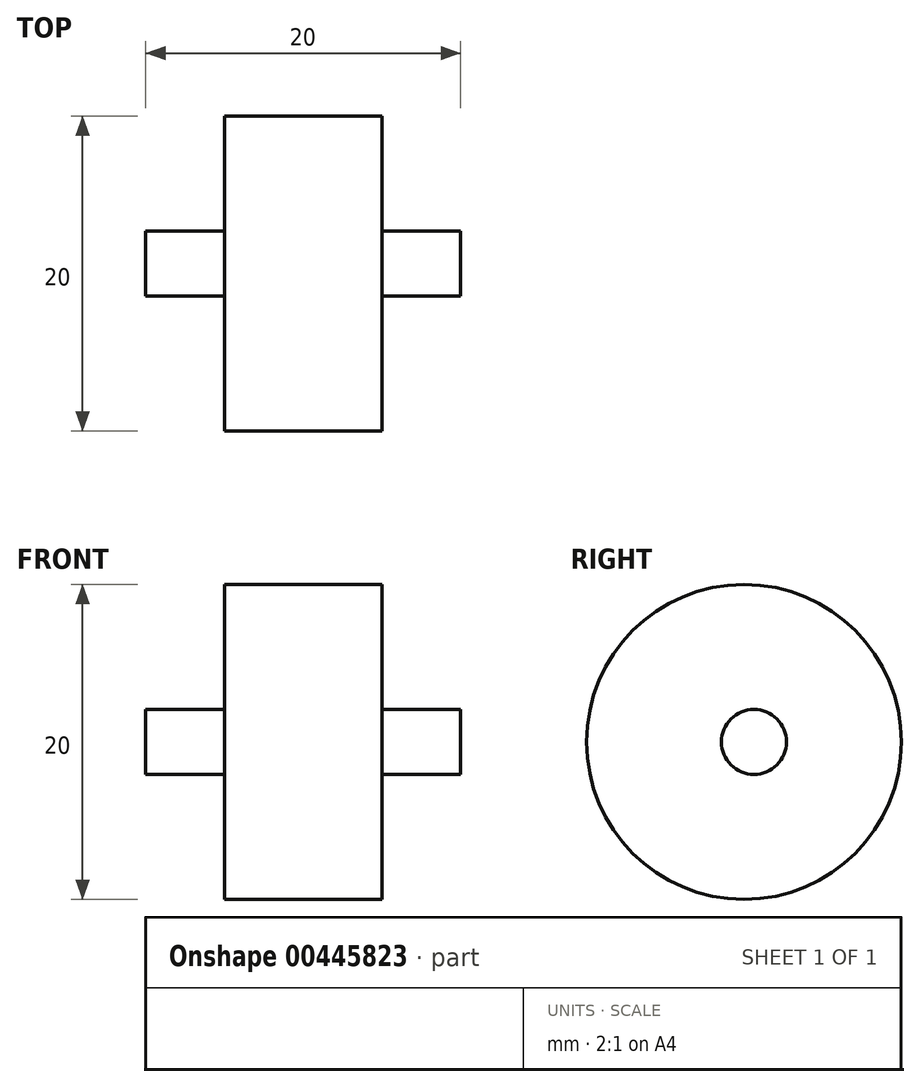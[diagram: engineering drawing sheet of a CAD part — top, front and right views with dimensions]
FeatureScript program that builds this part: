
annotation { "Feature Type Name" : "Feature", "Feature Type Description" : "" }
export const myFeature = defineFeature(function(context is Context, id is Id, definition is map)
    precondition{}
    {
        {
            var Q0;
            Q0=qCreatedBy(makeId("Right.planeOp"),FACE);
            var sketch = newSketch(context, id + "F0", { "sketchPlane" : qUnion([Q0])});
            skCircle(sketch, "E0", {"center": v(24.77, 0) * mm, "radius": 10 * mm});
            skSolve(sketch);
        }
        {
            var Q0;
            Q0=makeQuery(id+"F0.imprint","IMPRINT",FACE,{"disambiguationData":[TD([[makeQuery(id+"F0.imprint","IMPRINT",EDGE,{"derivedFrom":sQuery(id+"F0.wireOp",EDGE,"E0")}),1.0]])]});
            extrude(context, id + "F1", {"entities" : qUnion([Q0]), "endBound" : BoundingType.SYMMETRIC, "depth" : 10 * mm});
        }
        {
            var Q0;
            Q0=qCreatedBy(makeId("Right.planeOp"),FACE);
            var sketch = newSketch(context, id + "F2", { "sketchPlane" : qUnion([Q0])});
            skCircle(sketch, "E1", {"center": v(25.4, 0) * mm, "radius": 2.07 * mm});
            skSolve(sketch);
        }
        {
            var Q0;
            Q0=makeQuery(id+"F2.imprint","IMPRINT",FACE,{"disambiguationData":[TD([[makeQuery(id+"F2.imprint","IMPRINT",EDGE,{"derivedFrom":sQuery(id+"F2.wireOp",EDGE,"E1")}),1.0]])]});
            extrude(context, id + "F3", {"entities" : qUnion([Q0]), "operationType" : NewBodyOperationType.ADD, "endBound" : BoundingType.SYMMETRIC, "depth" : 20 * mm});
        }
    });
